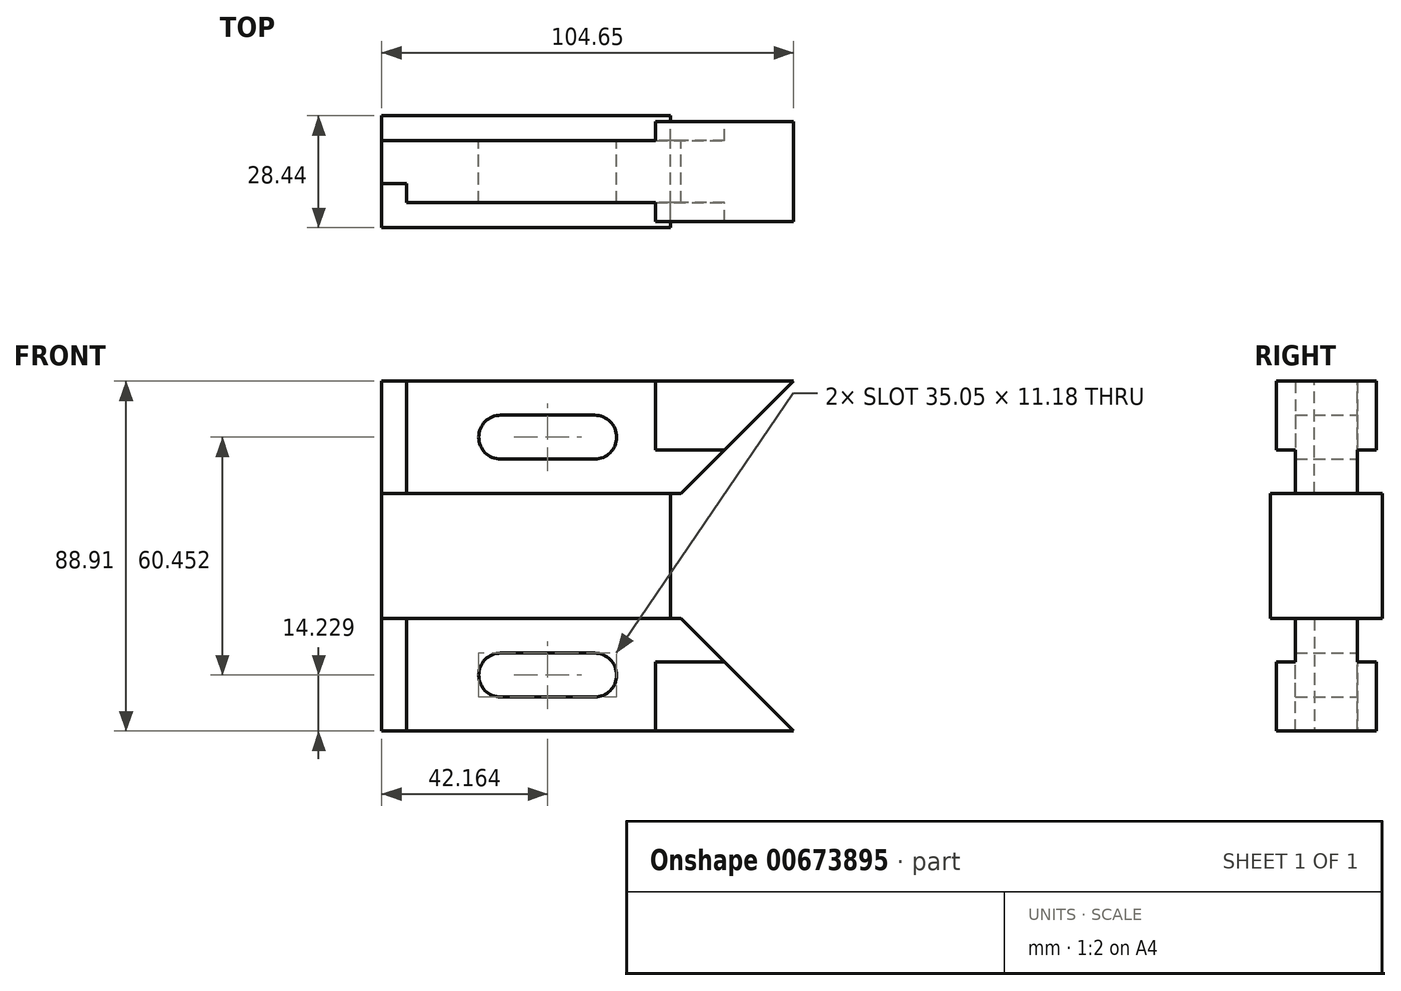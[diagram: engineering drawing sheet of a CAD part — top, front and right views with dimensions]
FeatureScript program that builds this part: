
annotation { "Feature Type Name" : "Feature", "Feature Type Description" : "" }
export const myFeature = defineFeature(function(context is Context, id is Id, definition is map)
    precondition{}
    {
        {
            var Q0;
            Q0=qCreatedBy(makeId("Front.planeOp"),FACE);
            var sketch = newSketch(context, id + "F0", { "sketchPlane" : qUnion([Q0])});
            skLineSegment(sketch, "E0.bottom", {"start": v(76.07, 0) * mm, "end": v(0, 0) * mm});
            skLineSegment(sketch, "E0.top", {"start": v(104.65, 28.58) * mm, "end": v(0, 28.58) * mm});
            skLineSegment(sketch, "E0.right", {"start": v(0, 0) * mm, "end": v(0, 28.58) * mm});
            skLineSegment(sketch, "E1", {"start": v(69.6, 11.05) * mm, "end": v(87.12, 11.05) * mm});
            skLineSegment(sketch, "E2", {"start": v(69.6, 28.58) * mm, "end": v(69.6, 11.05) * mm});
            skLineSegment(sketch, "E3", {"start": v(104.65, 28.58) * mm, "end": v(76.07, 0) * mm});
            skLineSegment(sketch, "E4.bottom", {"start": v(0, 0) * mm, "end": v(73.4, 0) * mm});
            skLineSegment(sketch, "E4.top", {"start": v(0, -15.87) * mm, "end": v(73.4, -15.87) * mm});
            skLineSegment(sketch, "E4.left", {"start": v(0, 0) * mm, "end": v(0, -15.87) * mm});
            skLineSegment(sketch, "E4.right", {"start": v(73.4, 0) * mm, "end": v(73.4, -15.87) * mm});
            skLineSegment(sketch, "E5", {"start": v(6.35, 28.57) * mm, "end": v(6.35, 0) * mm});
            skLineSegment(sketch, "E6.bottom", {"start": v(30.23, 19.94) * mm, "end": v(54.1, 19.94) * mm});
            skLineSegment(sketch, "E6.top", {"start": v(30.23, 8.76) * mm, "end": v(54.1, 8.76) * mm});
            skPoint(sketch, "E6.middle", {"position": v(42.16, 14.35) * mm});
            skArc(sketch, "E7", {"start": v(30.23, 19.94) * mm, "mid": v(24.64, 14.35) * mm, "end": v(30.23, 8.76) * mm});
            skArc(sketch, "E8", {"start": v(54.1, 8.76) * mm, "mid": v(59.7, 14.35) * mm, "end": v(54.1, 19.94) * mm});
            skPoint(sketch, "E9.orphan", {"position": v(24.64, 19.94) * mm});
            skPoint(sketch, "E10.orphan", {"position": v(24.64, 8.76) * mm});
            skPoint(sketch, "E11.orphan", {"position": v(59.69, 19.94) * mm});
            skPoint(sketch, "E12.orphan", {"position": v(59.69, 8.76) * mm});
            skPoint(sketch, "E13.start.orphan", {"position": v(15.76, 14.35) * mm});
            skPoint(sketch, "E14.orphan", {"position": v(68.57, 14.35) * mm});
            skSolve(sketch);
        }
        {
            var Q0;
            Q0=makeQuery(id+"F0.imprint","IMPRINT",FACE,{"disambiguationData":[TD([[makeQuery(id+"F0.imprint","IMPRINT",EDGE,{"derivedFrom":sQuery(id+"F0.wireOp",EDGE,"E4.top")}),1.0]])]});
            extrude(context, id + "F1", {"entities" : qUnion([Q0]), "endBound" : BoundingType.SYMMETRIC, "depth" : 28.45 * mm, "offsetDistance" : 25.4 * mm});
        }
        {
            var Q0;
            {var subQ2=sQuery(id+"F0.wireOp",EDGE,"E0.bottom");Q0=makeQuery(id+"F0.imprint","IMPRINT",FACE,{"disambiguationData":[TD([[makeQuery(id+"F0.imprint","IMPRINT",EDGE,{"derivedFrom":subQ2}),-1.0]])]});}
            extrude(context, id + "F2", {"entities" : qUnion([Q0]), "operationType" : NewBodyOperationType.ADD, "endBound" : BoundingType.SYMMETRIC, "depth" : 15.75 * mm, "offsetDistance" : 25.4 * mm});
        }
        {
            var Q0;
            {var subQ4=sQuery(id+"F0.wireOp",EDGE,"E1");Q0=makeQuery(id+"F0.imprint","IMPRINT",FACE,{"disambiguationData":[TD([[makeQuery(id+"F0.imprint","IMPRINT",EDGE,{"derivedFrom":subQ4}),1.0]])]});}
            extrude(context, id + "F3", {"entities" : qUnion([Q0]), "operationType" : NewBodyOperationType.ADD, "endBound" : BoundingType.SYMMETRIC, "depth" : 25.4 * mm, "offsetDistance" : 25.4 * mm});
        }
        {
            var Q0;
            {var subQ0=sQuery(id+"F0.wireOp",EDGE,"E0.right");Q0=makeQuery(id+"F0.imprint","IMPRINT",FACE,{"disambiguationData":[TD([[makeQuery(id+"F0.imprint","IMPRINT",EDGE,{"derivedFrom":subQ0}),-1.0]])]});}
            extrude(context, id + "F4", {"entities" : qUnion([Q0]), "operationType" : NewBodyOperationType.ADD, "depth" : 3.05 * mm, "offsetDistance" : 25.4 * mm, "hasSecondDirection" : true, "secondDirectionOppositeDirection" : true, "secondDirectionDepth" : 7.87 * mm});
        }
        {
            var Q0;
            Q0=makeQuery(id+"F1.opExtrude","SWEPT_BODY",BODY,{"disambiguationData":[OSD([sQuery(id+"F0.wireOp",EDGE,"E4.bottom"),sQuery(id+"F0.wireOp",EDGE,"E4.top"),sQuery(id+"F0.wireOp",EDGE,"E4.left"),sQuery(id+"F0.wireOp",EDGE,"E4.right")])]});
            var Q1;
            Q1=makeQuery(id+"F1.opExtrude","SWEPT_FACE",FACE,{"disambiguationData":[OSD([sQuery(id+"F0.wireOp",EDGE,"E4.top")])]});
            mirror(context, id + "F5", {"operationType" : NewBodyOperationType.ADD, "entities" : qUnion([Q0]), "mirrorPlane" : qUnion([Q1])});
        }
    });
